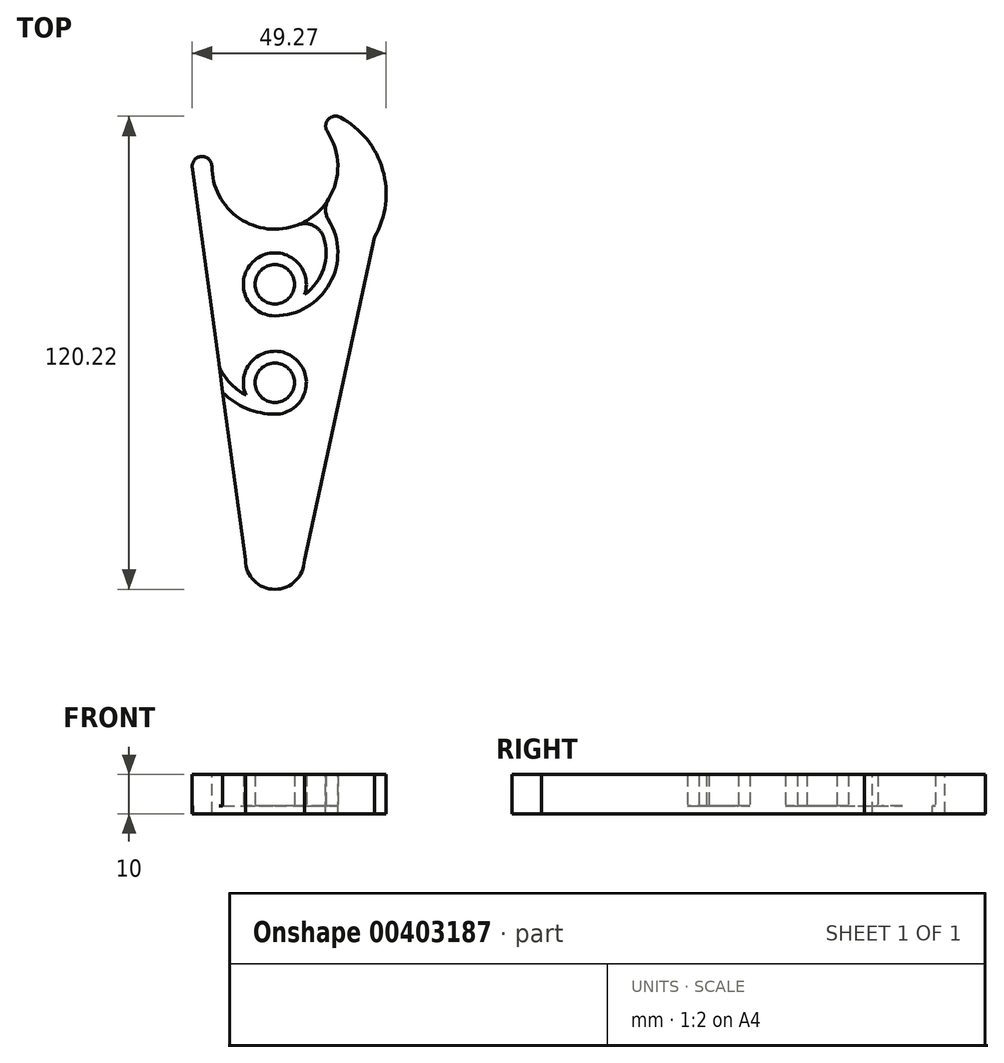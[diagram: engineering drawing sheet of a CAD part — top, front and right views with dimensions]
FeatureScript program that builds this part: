
annotation { "Feature Type Name" : "Feature", "Feature Type Description" : "" }
export const myFeature = defineFeature(function(context is Context, id is Id, definition is map)
    precondition{}
    {
        {
            var Q0;
            Q0=qCreatedBy(makeId("Top.planeOp"),FACE);
            var sketch = newSketch(context, id + "F0", { "sketchPlane" : qUnion([Q0])});
            skArc(sketch, "E0", {"start": v(-7.5, -100) * mm, "mid": v(0, -107.5) * mm, "end": v(7.5, -100) * mm});
            skLineSegment(sketch, "E1", {"start": v(-7.5, -100) * mm, "end": v(-13.24, -57.44) * mm});
            skArc(sketch, "E2", {"start": v(-16, 0) * mm, "mid": v(-9.03, -13.2) * mm, "end": v(5.8, -14.9) * mm});
            skArc(sketch, "E3", {"start": v(25.3, -18.03) * mm, "mid": v(27.42, -0.95) * mm, "end": v(16.6, 12.43) * mm});
            skArc(sketch, "E4", {"start": v(-16, 0) * mm, "mid": v(-18.5, 2.5) * mm, "end": v(-21, 0) * mm});
            skArc(sketch, "E5", {"start": v(16.6, 12.43) * mm, "mid": v(13.57, 11.9) * mm, "end": v(13.34, 8.84) * mm});
            skLineSegment(sketch, "E6", {"start": v(7.5, -100) * mm, "end": v(25.3, -18.03) * mm});
            skCircle(sketch, "E7", {"center": v(0, -30) * mm, "radius": 5 * mm});
            skArc(sketch, "E8", {"start": v(7.58, -32.56) * mm, "mid": v(-4.66, -23.5) * mm, "end": v(0, -38) * mm});
            skArc(sketch, "E9", {"start": v(0, -38) * mm, "mid": v(13.97, -29.8) * mm, "end": v(13.63, -13.62) * mm});
            skArc(sketch, "E10.trimOffspring", {"start": v(7.58, -32.56) * mm, "mid": v(12.34, -26.09) * mm, "end": v(12.38, -18.05) * mm});
            skArc(sketch, "E11.trimOffspring", {"start": v(13.63, -8.38) * mm, "mid": v(16, 0.27) * mm, "end": v(13.34, 8.84) * mm});
            skPoint(sketch, "E12.visualSharp", {"position": v(11.62, -11) * mm});
            skArc(sketch, "E12.filletArc", {"start": v(13.63, -8.38) * mm, "mid": v(12.89, -11) * mm, "end": v(13.63, -13.62) * mm});
            skPoint(sketch, "E13.visualSharp", {"position": v(9.36, -12.98) * mm});
            skArc(sketch, "E13.filletArc", {"start": v(12.38, -18.05) * mm, "mid": v(9.77, -15.06) * mm, "end": v(5.8, -14.9) * mm});
            skCircle(sketch, "E14", {"center": v(0, -55) * mm, "radius": 5 * mm});
            skArc(sketch, "E15", {"start": v(0, -63) * mm, "mid": v(4.4, -48.32) * mm, "end": v(-7.35, -58.15) * mm});
            skArc(sketch, "E16", {"start": v(-13.66, -51.9) * mm, "mid": v(-10.96, -55.49) * mm, "end": v(-7.35, -58.15) * mm});
            skArc(sketch, "E17.trimOffspring", {"start": v(-13.24, -57.44) * mm, "mid": v(-7.18, -61.55) * mm, "end": v(0, -63) * mm});
            skLineSegment(sketch, "E18.trimOffspring", {"start": v(-14.23, -50.17) * mm, "end": v(-21, 0) * mm});
            skPoint(sketch, "E19.visualSharp", {"position": v(-14.12, -51) * mm});
            skArc(sketch, "E19.filletArc", {"start": v(-14.23, -50.17) * mm, "mid": v(-14.02, -51.06) * mm, "end": v(-13.66, -51.9) * mm});
            skSolve(sketch);
        }
        {
            var Q0;
            Q0=qCreatedBy(makeId("Top.planeOp"),FACE);
            var sketch = newSketch(context, id + "F1", { "sketchPlane" : qUnion([Q0])});
            skArc(sketch, "E20", {"start": v(-16, 0) * mm, "mid": v(4.62, -15.32) * mm, "end": v(13.34, 8.84) * mm});
            skArc(sketch, "E21", {"start": v(25.3, -18.03) * mm, "mid": v(27.42, -0.95) * mm, "end": v(16.6, 12.43) * mm});
            skArc(sketch, "E22", {"start": v(-16, 0) * mm, "mid": v(-18.83, 2.48) * mm, "end": v(-20.91, -0.66) * mm});
            skArc(sketch, "E23", {"start": v(16.6, 12.43) * mm, "mid": v(13.57, 11.9) * mm, "end": v(13.34, 8.84) * mm});
            skArc(sketch, "E24", {"start": v(-7.5, -100) * mm, "mid": v(0, -107.5) * mm, "end": v(7.5, -100) * mm});
            skLineSegment(sketch, "E25", {"start": v(-21, 0) * mm, "end": v(-7.5, -100) * mm});
            skLineSegment(sketch, "E26", {"start": v(7.5, -100) * mm, "end": v(25.3, -18.03) * mm});
            skSolve(sketch);
        }
        {
            var Q0;
            Q0 = qSketchRegion(id + "F1", true);
            extrude(context, id + "F2", {"entities" : qUnion([Q0]), "oppositeDirection" : true, "depth" : 2 * mm});
        }
        {
            var Q0;
            Q0 = qSketchRegion(id + "F0", true);
            extrude(context, id + "F3", {"entities" : qUnion([Q0]), "operationType" : NewBodyOperationType.ADD, "depth" : 8 * mm});
        }
    });
